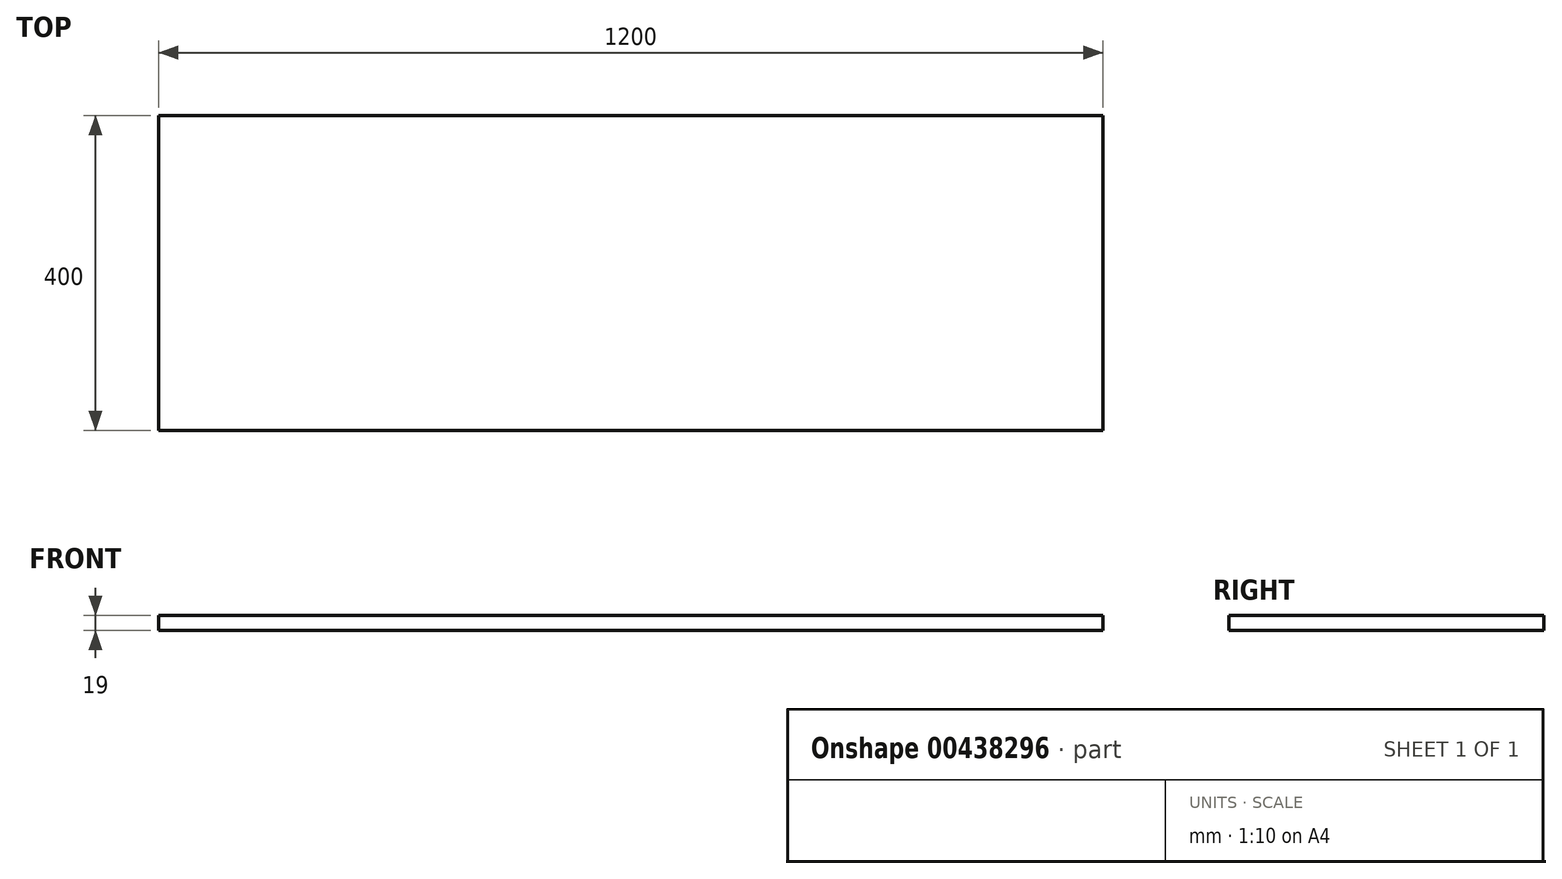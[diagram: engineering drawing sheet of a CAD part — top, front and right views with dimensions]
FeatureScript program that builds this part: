
annotation { "Feature Type Name" : "Feature", "Feature Type Description" : "" }
export const myFeature = defineFeature(function(context is Context, id is Id, definition is map)
    precondition{}
    {
        {
            var Q0;
            Q0=qCreatedBy(makeId("Top.planeOp"),FACE);
            var sketch = newSketch(context, id + "F0", { "sketchPlane" : qUnion([Q0])});
            skLineSegment(sketch, "E0.bottom", {"start": v(-592.04, -495.73) * mm, "end": v(607.96, -495.73) * mm});
            skLineSegment(sketch, "E0.top", {"start": v(-592.04, -95.73) * mm, "end": v(607.96, -95.73) * mm});
            skLineSegment(sketch, "E0.left", {"start": v(-592.04, -495.73) * mm, "end": v(-592.04, -95.73) * mm});
            skLineSegment(sketch, "E0.right", {"start": v(607.96, -495.73) * mm, "end": v(607.96, -95.73) * mm});
            skSolve(sketch);
        }
        {
            var Q0;
            Q0=makeQuery(id+"F0.imprint","IMPRINT",FACE,{"disambiguationData":[TD([[makeQuery(id+"F0.imprint","IMPRINT",EDGE,{"derivedFrom":sQuery(id+"F0.wireOp",EDGE,"E0.bottom")}),1.0]])]});
            extrude(context, id + "F1", {"entities" : qUnion([Q0]), "depth" : 19 * mm});
        }
    });
